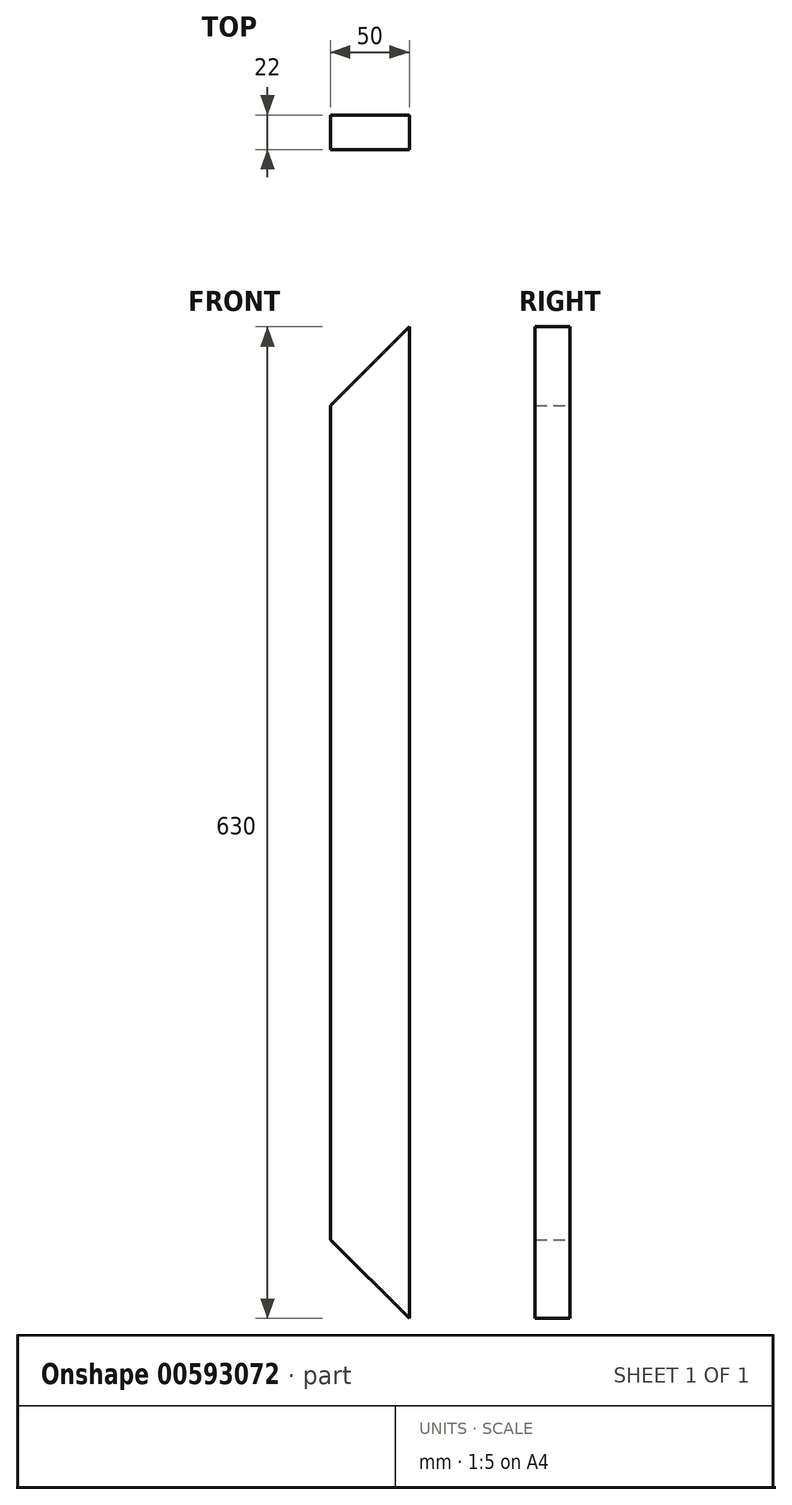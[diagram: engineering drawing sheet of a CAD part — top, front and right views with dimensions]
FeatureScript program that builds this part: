
annotation { "Feature Type Name" : "Feature", "Feature Type Description" : "" }
export const myFeature = defineFeature(function(context is Context, id is Id, definition is map)
    precondition{}
    {
        {
            var Q0;
            Q0=qCreatedBy(makeId("Front.planeOp"),FACE);
            var sketch = newSketch(context, id + "F0", { "sketchPlane" : qUnion([Q0])});
            skLineSegment(sketch, "E0.left", {"start": v(-50, 265) * mm, "end": v(-50, -265) * mm});
            skLineSegment(sketch, "E0.right", {"start": v(0, 315) * mm, "end": v(0, -315) * mm});
            skLineSegment(sketch, "E1", {"start": v(0, -315) * mm, "end": v(-50, -265) * mm});
            skLineSegment(sketch, "E2", {"start": v(0, 315) * mm, "end": v(-50, 265) * mm});
            skSolve(sketch);
        }
        {
            var Q0;
            Q0=makeQuery(id+"F0.imprint","IMPRINT",FACE,{"disambiguationData":[TD([[makeQuery(id+"F0.imprint","IMPRINT",EDGE,{"derivedFrom":sQuery(id+"F0.wireOp",EDGE,"E0.left")}),1.0]])]});
            extrude(context, id + "F1", {"entities" : qUnion([Q0]), "depth" : 22 * mm, "offsetDistance" : 25 * mm});
        }
    });
